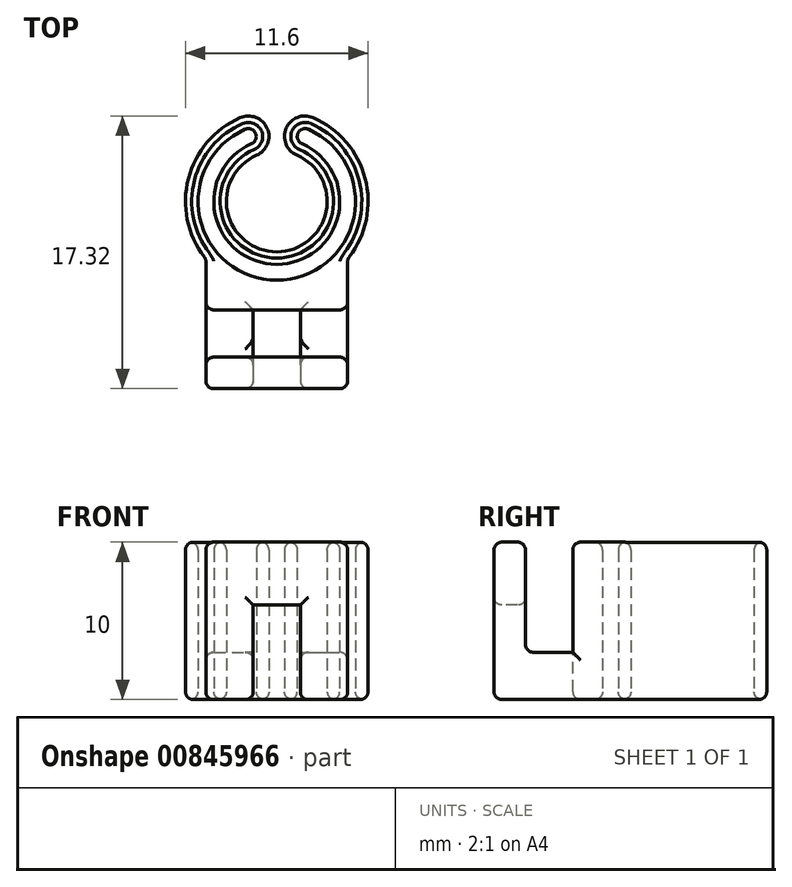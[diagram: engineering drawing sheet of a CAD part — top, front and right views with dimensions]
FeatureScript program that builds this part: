
annotation { "Feature Type Name" : "Feature", "Feature Type Description" : "" }
export const myFeature = defineFeature(function(context is Context, id is Id, definition is map)
    precondition{}
    {
        {
            var Q0;
            Q0=qCreatedBy(makeId("Top.planeOp"),FACE);
            var sketch = newSketch(context, id + "F0", { "sketchPlane" : qUnion([Q0])});
            skArc(sketch, "E0", {"start": v(-2.32, 5.32) * mm, "mid": v(0, -5.8) * mm, "end": v(2.3, 5.32) * mm});
            skArc(sketch, "E1", {"start": v(-1.28, 2.93) * mm, "mid": v(0, -3.2) * mm, "end": v(1.27, 2.94) * mm});
            skArc(sketch, "E2", {"start": v(-1.6, 3.67) * mm, "mid": v(0, -4) * mm, "end": v(1.6, 3.67) * mm});
            skArc(sketch, "E3", {"start": v(-2, 4.58) * mm, "mid": v(0, -5) * mm, "end": v(2, 4.58) * mm});
            skPoint(sketch, "E4.first.point", {"position": v(-2.32, 5.32) * mm});
            skPoint(sketch, "E4.third.point", {"position": v(-1.28, 2.93) * mm});
            skPoint(sketch, "E5.first.point", {"position": v(-2, 4.58) * mm});
            skPoint(sketch, "E5.third.point", {"position": v(-1.6, 3.67) * mm});
            skPoint(sketch, "E6.startSnap0", {"position": v(1.5, -4.77) * mm});
            skPoint(sketch, "E7.first.point", {"position": v(2.3, 5.32) * mm});
            skPoint(sketch, "E7.second.point", {"position": v(0.5, 4.03) * mm});
            skPoint(sketch, "E7.third.point", {"position": v(1.27, 2.94) * mm});
            skArc(sketch, "E8.trimOffspring", {"start": v(-0.7, 3.94) * mm, "mid": v(-0.71, 3.94) * mm, "end": v(-0.71, 3.94) * mm});
            skPoint(sketch, "E9.first.point", {"position": v(2, 4.58) * mm});
            skPoint(sketch, "E9.third.point", {"position": v(1.6, 3.67) * mm});
            skPoint(sketch, "E10.startSnap0", {"position": v(0, -5.8) * mm});
            skLineSegment(sketch, "E11", {"start": v(4.5, -5.89) * mm, "end": v(4.5, -3.66) * mm});
            skLineSegment(sketch, "E12", {"start": v(-4.5, -11.89) * mm, "end": v(4.5, -11.89) * mm});
            skLineSegment(sketch, "E13", {"start": v(4.5, -11.89) * mm, "end": v(4.5, -5.89) * mm});
            skArc(sketch, "E14", {"start": v(2.3, 5.32) * mm, "mid": v(0.6, 4.65) * mm, "end": v(1.27, 2.94) * mm});
            skPoint(sketch, "E14.second.point", {"position": v(0.5, 4.13) * mm});
            skLineSegment(sketch, "E15", {"start": v(-0.5, 4.1) * mm, "end": v(-0.5, 4.15) * mm, "construction": true});
            skArc(sketch, "E16", {"start": v(-1.28, 2.93) * mm, "mid": v(-0.6, 4.64) * mm, "end": v(-2.32, 5.32) * mm});
            skPoint(sketch, "E16.second.point", {"position": v(-0.5, 4.1) * mm});
            skArc(sketch, "E17", {"start": v(2, 4.58) * mm, "mid": v(1.34, 4.32) * mm, "end": v(1.6, 3.67) * mm});
            skPoint(sketch, "E17.second.point", {"position": v(1.3, 4.12) * mm});
            skLineSegment(sketch, "E18", {"start": v(2, 4.58) * mm, "end": v(2, 4.58) * mm});
            skLineSegment(sketch, "E19", {"start": v(1.6, 3.67) * mm, "end": v(1.6, 3.67) * mm});
            skArc(sketch, "E20", {"start": v(-1.6, 3.67) * mm, "mid": v(-1.34, 4.32) * mm, "end": v(-2, 4.58) * mm});
            skPoint(sketch, "E20.second.point", {"position": v(-1.3, 4.12) * mm});
            skPoint(sketch, "E21.start.orphan", {"position": v(-1.3, 0) * mm});
            skPoint(sketch, "E22.orphan", {"position": v(0.5, 0) * mm});
            skPoint(sketch, "E23.orphan", {"position": v(1.3, 0) * mm});
            skLineSegment(sketch, "E24", {"start": v(0, 0) * mm, "end": v(0, -15) * mm, "construction": true});
            skPoint(sketch, "E25.start.orphan", {"position": v(-4.35, -5.8) * mm});
            skLineSegment(sketch, "E26", {"start": v(-4.5, -11.89) * mm, "end": v(-4.5, -3.66) * mm});
            skSolve(sketch);
        }
        {
            var Q0;
            {var subQ4=sQuery(id+"F0.wireOp",EDGE,"E1");Q0=makeQuery(id+"F0.imprint","IMPRINT",FACE,{"disambiguationData":[TD([[makeQuery(id+"F0.imprint","IMPRINT",EDGE,{"derivedFrom":subQ4}),-1.0]])]});}
            var Q1;
            {var subQ0=sQuery(id+"F0.wireOp",EDGE,"3bprE6z8-PvV8-sgfb-jGKl-TbjKrrVLwJ7d");Q1=makeQuery(id+"F0.imprint","IMPRINT",FACE,{"disambiguationData":[TD([[makeQuery(id+"F0.imprint","IMPRINT",EDGE,{"derivedFrom":subQ0}),-1.0]])]});}
            var Q2;
            {var subQ0=sQuery(id+"F0.wireOp",EDGE,"E11");Q2=makeQuery(id+"F0.imprint","IMPRINT",FACE,{"disambiguationData":[TD([[makeQuery(id+"F0.imprint","IMPRINT",EDGE,{"derivedFrom":subQ0}),1.0]])]});}
            extrude(context, id + "F1", {"entities" : qUnion([Q0, Q1, Q2]), "depth" : 10 * mm, "offsetDistance" : 25 * mm});
        }
        {
            var Q0;
            Q0=makeQuery(id+"F1.opExtrude","CAP_FACE",FACE,{"disambiguationData":[OSD([sQuery(id+"F0.wireOp",EDGE,"E0"),sQuery(id+"F0.wireOp",EDGE,"E1"),sQuery(id+"F0.wireOp",EDGE,"E2"),sQuery(id+"F0.wireOp",EDGE,"E3"),sQuery(id+"F0.wireOp",EDGE,"E4"),sQuery(id+"F0.wireOp",EDGE,"E5"),sQuery(id+"F0.wireOp",EDGE,"67d27ae3-ba20-4222-b287-de2d1b690a39.trimOffspring"),sQuery(id+"F0.wireOp",EDGE,"E9"),sQuery(id+"F0.wireOp",EDGE,"3bprE6z8-PvV8-sgfb-jGKl-TbjKrrVLwJ7d"),sQuery(id+"F0.wireOp",EDGE,"E11"),sQuery(id+"F0.wireOp",EDGE,"E25"),sQuery(id+"F0.wireOp",EDGE,"E12"),sQuery(id+"F0.wireOp",EDGE,"E13")])],"isStart":false});
            var sketch = newSketch(context, id + "F2", { "sketchPlane" : qUnion([Q0])});
            skLineSegment(sketch, "E27.bottom", {"start": v(-4.5, -9.89) * mm, "end": v(4.5, -9.89) * mm});
            skLineSegment(sketch, "E27.top", {"start": v(-4.5, -6.89) * mm, "end": v(4.5, -6.89) * mm});
            skLineSegment(sketch, "E27.left", {"start": v(-4.5, -9.89) * mm, "end": v(-4.5, -6.89) * mm});
            skLineSegment(sketch, "E27.right", {"start": v(4.5, -9.89) * mm, "end": v(4.5, -6.89) * mm});
            skSolve(sketch);
        }
        {
            var Q0;
            Q0=makeQuery(id+"F2.imprint","IMPRINT",FACE,{"disambiguationData":[TD([[makeQuery(id+"F2.imprint","IMPRINT",EDGE,{"derivedFrom":sQuery(id+"F2.wireOp",EDGE,"E27.bottom")}),1.0]])]});
            extrude(context, id + "F3", {"entities" : qUnion([Q0]), "operationType" : NewBodyOperationType.REMOVE, "oppositeDirection" : true, "depth" : 7 * mm, "offsetDistance" : 25 * mm});
        }
        {
            var Q0;
            Q0=makeQuery(id+"F1.opExtrude","SWEPT_FACE",FACE,{"disambiguationData":[OSD([sQuery(id+"F0.wireOp",EDGE,"E12")])]});
            var sketch = newSketch(context, id + "F4", { "sketchPlane" : qUnion([Q0])});
            skLineSegment(sketch, "E28.bottom", {"start": v(-1.5, 0) * mm, "end": v(1.5, 0) * mm});
            skLineSegment(sketch, "E28.top", {"start": v(-1.5, 6) * mm, "end": v(1.5, 6) * mm});
            skLineSegment(sketch, "E28.left", {"start": v(-1.5, 0) * mm, "end": v(-1.5, 6) * mm});
            skLineSegment(sketch, "E28.right", {"start": v(1.5, 0) * mm, "end": v(1.5, 6) * mm});
            skSolve(sketch);
        }
        {
            var Q0;
            Q0=makeQuery(id+"F4.imprint","IMPRINT",FACE,{"disambiguationData":[TD([[makeQuery(id+"F4.imprint","IMPRINT",EDGE,{"derivedFrom":sQuery(id+"F4.wireOp",EDGE,"E28.bottom")}),1.0]])]});
            extrude(context, id + "F5", {"entities" : qUnion([Q0]), "operationType" : NewBodyOperationType.REMOVE, "oppositeDirection" : true, "depth" : 5 * mm, "offsetDistance" : 25 * mm});
        }
        {
            var Q0;
            {var subQ0=sQuery(id+"F0.wireOp",EDGE,"E20");var subQ1=sQuery(id+"F0.wireOp",EDGE,"E16");var subQ2=sQuery(id+"F0.wireOp",EDGE,"E14");var subQ3=sQuery(id+"F0.wireOp",EDGE,"E2");var subQ4=sQuery(id+"F0.wireOp",EDGE,"E13");var subQ5=sQuery(id+"F0.wireOp",EDGE,"E11");var subQ6=sQuery(id+"F0.wireOp",EDGE,"E17");var subQ7=sQuery(id+"F0.wireOp",EDGE,"E0");var subQ8=sQuery(id+"F0.wireOp",EDGE,"E26");var subQ9=sQuery(id+"F0.wireOp",EDGE,"E3");var subQ10=sQuery(id+"F0.wireOp",EDGE,"E1");Q0=makeQuery(id+"F3.boolean.opBoolean","SPLIT",FACE,{"disambiguationData":[TD([makeQuery(id+"F1.opExtrude","SWEPT_FACE",FACE,{"disambiguationData":[OSD([subQ10])]})])],"derivedFrom":makeQuery(id+"F1.opExtrude","CAP_FACE",FACE,{"disambiguationData":[OSD([subQ7,subQ10,subQ9,subQ5,sQuery(id+"F0.wireOp",EDGE,"E12"),subQ4,subQ3,subQ2,subQ1,subQ6,subQ0,subQ8])],"isStart":false})});}
            var Q1;
            Q1=makeQuery(id+"F1.opExtrude","SWEPT_FACE",FACE,{"disambiguationData":[OSD([sQuery(id+"F0.wireOp",EDGE,"E11"),sQuery(id+"F0.wireOp",EDGE,"E13")])]});
            var Q2;
            Q2=makeQuery(id+"F1.opExtrude","SWEPT_FACE",FACE,{"disambiguationData":[OSD([sQuery(id+"F0.wireOp",EDGE,"E26")])]});
            var Q3;
            Q3=makeQuery(id+"F1.opExtrude","CAP_FACE",FACE,{"disambiguationData":[OSD([sQuery(id+"F0.wireOp",EDGE,"E0"),sQuery(id+"F0.wireOp",EDGE,"E1"),sQuery(id+"F0.wireOp",EDGE,"E3"),sQuery(id+"F0.wireOp",EDGE,"E11"),sQuery(id+"F0.wireOp",EDGE,"E12"),sQuery(id+"F0.wireOp",EDGE,"E13"),sQuery(id+"F0.wireOp",EDGE,"E2"),sQuery(id+"F0.wireOp",EDGE,"E14"),sQuery(id+"F0.wireOp",EDGE,"E16"),sQuery(id+"F0.wireOp",EDGE,"E17"),sQuery(id+"F0.wireOp",EDGE,"E20"),sQuery(id+"F0.wireOp",EDGE,"E26")])],"isStart":true});
            var Q4;
            Q4=makeQuery(id+"F1.opExtrude","SWEPT_FACE",FACE,{"disambiguationData":[OSD([sQuery(id+"F0.wireOp",EDGE,"E12")])]});
            var Q5;
            Q5=makeQuery(id+"F3.boolean.opBoolean","COPY",FACE,{"derivedFrom":makeQuery(id+"F3.opExtrude","SWEPT_FACE",FACE,{"disambiguationData":[OSD([sQuery(id+"F2.wireOp",EDGE,"E27.bottom")])]})});
            fillet(context, id + "F6", {"entities" : qUnion([Q0, Q1, Q2, Q3, Q4, Q5]), "radius" : .5 * mm, "tangentPropagation" : true, "allowEdgeOverflow" : false});
        }
    });
